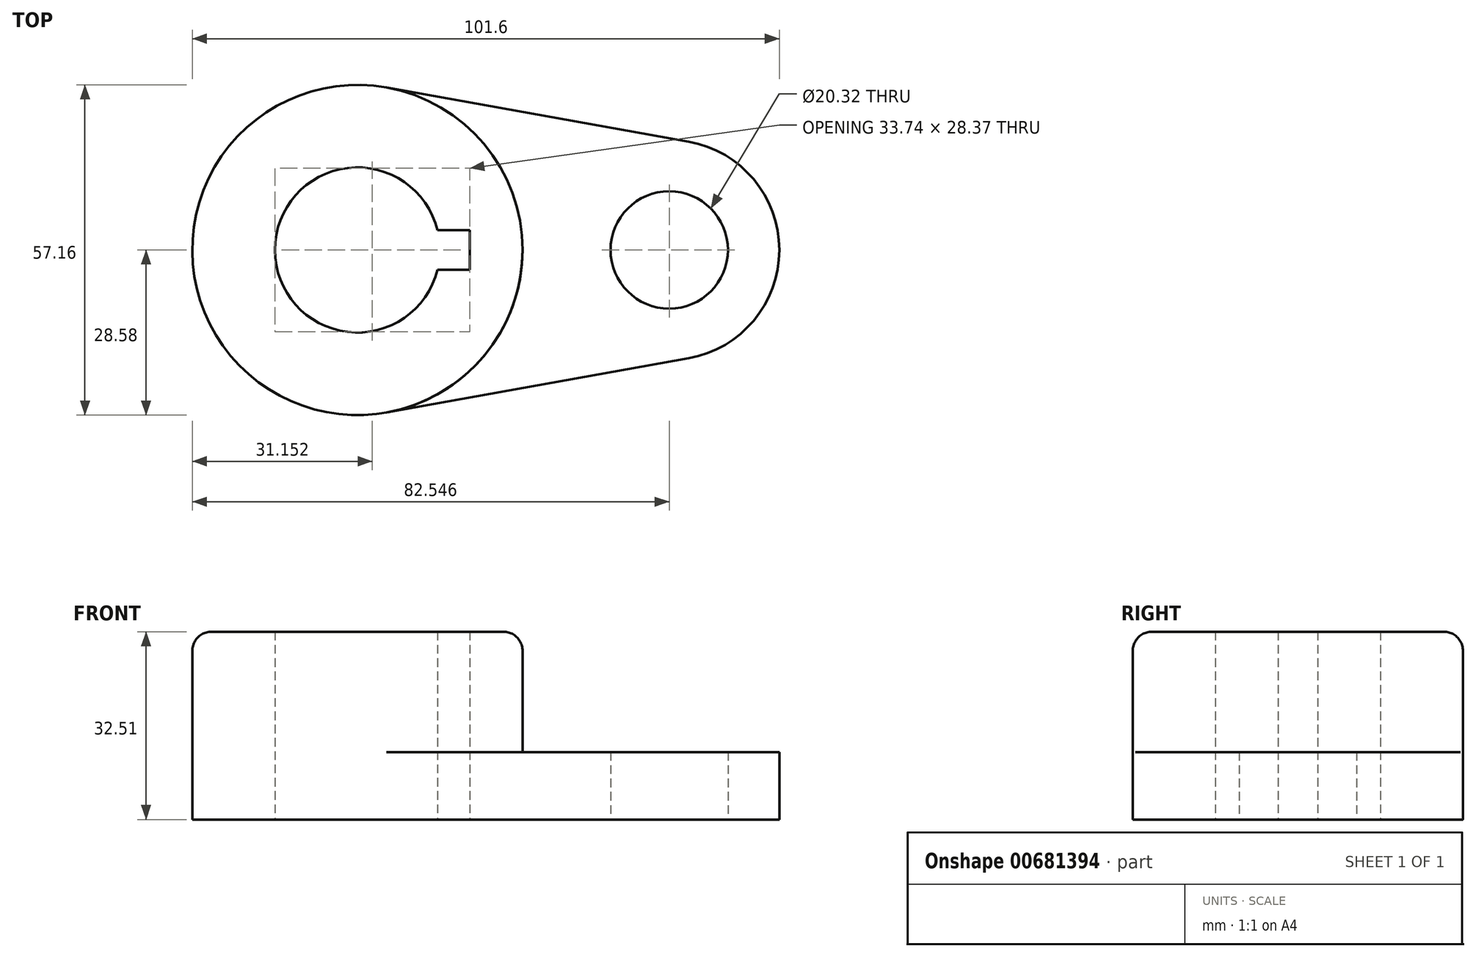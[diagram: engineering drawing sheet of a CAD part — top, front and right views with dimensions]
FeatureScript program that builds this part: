
annotation { "Feature Type Name" : "Feature", "Feature Type Description" : "" }
export const myFeature = defineFeature(function(context is Context, id is Id, definition is map)
    precondition{}
    {
        {
            var Q0;
            Q0=qCreatedBy(makeId("Top.planeOp"),FACE);
            var sketch = newSketch(context, id + "F0", { "sketchPlane" : qUnion([Q0])});
            skCircle(sketch, "E0", {"center": v(34.53, 0) * mm, "radius": 10.16 * mm});
            skLineSegment(sketch, "E1", {"start": v(34.53, 0) * mm, "end": v(-19.45, 0) * mm});
            skCircle(sketch, "E2", {"center": v(-19.45, 0) * mm, "radius": 14.29 * mm});
            skCircle(sketch, "E3", {"center": v(-19.45, 0) * mm, "radius": 28.58 * mm});
            skCircle(sketch, "E4", {"center": v(-19.45, 0) * mm, "radius": 24.87 * mm});
            skLineSegment(sketch, "E5.bottom", {"start": v(0, -3.41) * mm, "end": v(-33.32, -3.41) * mm});
            skLineSegment(sketch, "E5.top", {"start": v(0, 3.41) * mm, "end": v(-33.32, 3.41) * mm});
            skLineSegment(sketch, "E5.left", {"start": v(0, -3.41) * mm, "end": v(0, 3.41) * mm});
            skPoint(sketch, "E5.right.end.orphan", {"position": v(-38.9, 3.41) * mm});
            skPoint(sketch, "E6.orphan", {"position": v(-38.9, -3.41) * mm});
            skArc(sketch, "E7", {"start": v(37.89, -18.75) * mm, "mid": v(53.58, 0) * mm, "end": v(37.89, 18.75) * mm});
            skLineSegment(sketch, "E8", {"start": v(-14.4, 28.13) * mm, "end": v(37.89, 18.75) * mm});
            skLineSegment(sketch, "E9", {"start": v(-14.4, -28.13) * mm, "end": v(37.89, -18.75) * mm});
            skSolve(sketch);
        }
        {
            var Q0;
            Q0=makeQuery(id+"F0.imprint","IMPRINT",FACE,{"disambiguationData":[TD([[makeQuery(id+"F0.imprint","IMPRINT",EDGE,{"derivedFrom":sQuery(id+"F0.wireOp",EDGE,"E4")}),1.0]])]});
            var Q1;
            Q1=makeQuery(id+"F0.imprint","IMPRINT",FACE,{"disambiguationData":[TD([[makeQuery(id+"F0.imprint","IMPRINT",EDGE,{"derivedFrom":sQuery(id+"F0.wireOp",EDGE,"E4")}),-1.0]])]});
            extrude(context, id + "F1", {"entities" : qUnion([Q0, Q1]), "depth" : 32.5 * mm, "offsetDistance" : 25.4 * mm});
        }
        {
            var Q0;
            Q0=qSketchRegion(id+"F0",true);
            extrude(context, id + "F2", {"entities" : qUnion([Q0]), "operationType" : NewBodyOperationType.ADD, "depth" : 11.68 * mm, "offsetDistance" : 25.4 * mm});
        }
        {
            var Q0;
            Q0=makeQuery(id+"F1.opExtrude","CAP_EDGE",EDGE,{"disambiguationData":[OSD([sQuery(id+"F0.wireOp",EDGE,"E3")])],"isStart":false});
            fillet(context, id + "F3", {"entities" : qUnion([Q0]), "radius" : 3.3 * mm, "tangentPropagation" : true, "allowEdgeOverflow" : false});
        }
    });
